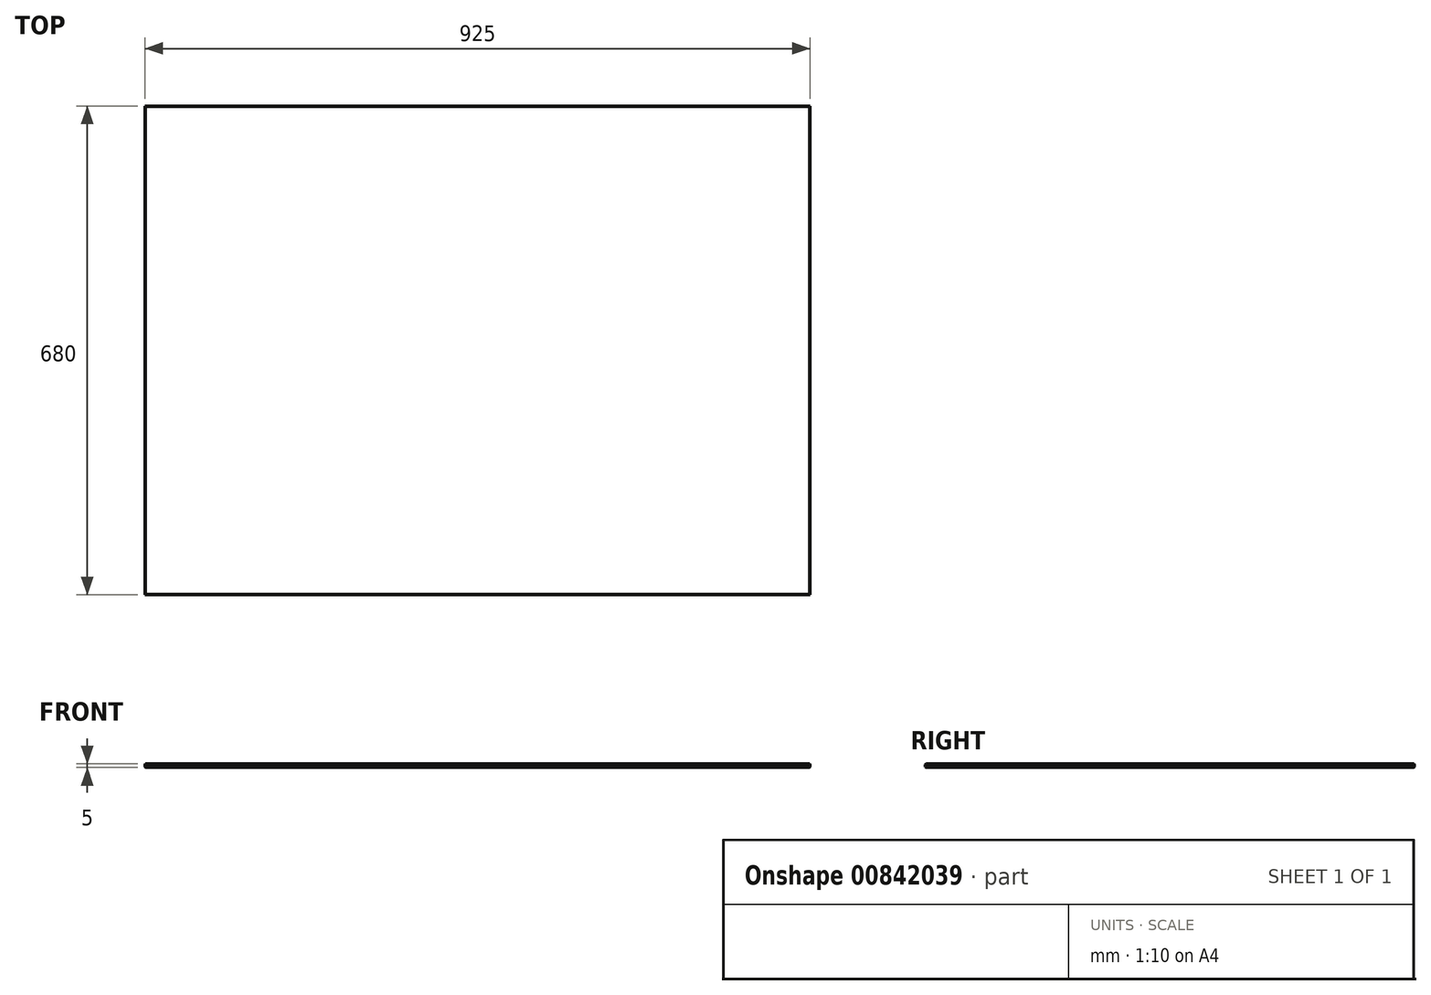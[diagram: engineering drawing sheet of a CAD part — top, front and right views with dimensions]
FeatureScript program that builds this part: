
annotation { "Feature Type Name" : "Feature", "Feature Type Description" : "" }
export const myFeature = defineFeature(function(context is Context, id is Id, definition is map)
    precondition{}
    {
        {
            var Q0;
            Q0=qCreatedBy(makeId("Top.planeOp"),FACE);
            var sketch = newSketch(context, id + "F0", { "sketchPlane" : qUnion([Q0])});
            skLineSegment(sketch, "E0.bottom", {"start": v(-462.5, 340) * mm, "end": v(462.5, 340) * mm});
            skLineSegment(sketch, "E0.top", {"start": v(-462.5, -340) * mm, "end": v(462.5, -340) * mm});
            skLineSegment(sketch, "E0.left", {"start": v(-462.5, 340) * mm, "end": v(-462.5, -340) * mm});
            skLineSegment(sketch, "E0.right", {"start": v(462.5, 340) * mm, "end": v(462.5, -340) * mm});
            skPoint(sketch, "E0.middle", {"position": v(0, 0) * mm});
            skSolve(sketch);
        }
        {
            var Q0;
            Q0=makeQuery(id+"F0.imprint","IMPRINT",FACE,{"disambiguationData":[TD([[makeQuery(id+"F0.imprint","IMPRINT",EDGE,{"derivedFrom":sQuery(id+"F0.wireOp",EDGE,"E0.bottom")}),-1.0]])]});
            extrude(context, id + "F1", {"entities" : qUnion([Q0]), "endBound" : BoundingType.SYMMETRIC, "depth" : 5 * mm, "offsetDistance" : 25 * mm});
        }
        {
            var Q0;
            Q0=makeQuery(id+"F1.opExtrude","CAP_EDGE",EDGE,{"disambiguationData":[OSD([sQuery(id+"F0.wireOp",EDGE,"E0.top")])],"isStart":false});
            var Q1;
            Q1=makeQuery(id+"F1.opExtrude","CAP_EDGE",EDGE,{"disambiguationData":[OSD([sQuery(id+"F0.wireOp",EDGE,"E0.right")])],"isStart":false});
            var Q2;
            Q2=makeQuery(id+"F1.opExtrude","CAP_EDGE",EDGE,{"disambiguationData":[OSD([sQuery(id+"F0.wireOp",EDGE,"E0.bottom")])],"isStart":false});
            var Q3;
            Q3=makeQuery(id+"F1.opExtrude","CAP_EDGE",EDGE,{"disambiguationData":[OSD([sQuery(id+"F0.wireOp",EDGE,"E0.left")])],"isStart":false});
            chamfer(context, id + "F2", {"entities" : qUnion([Q0, Q1, Q2, Q3]), "width" : 1 * mm, "tangentPropagation" : true});
        }
        {
            var Q0;
            Q0=makeQuery(id+"F1.opExtrude","CAP_EDGE",EDGE,{"disambiguationData":[OSD([sQuery(id+"F0.wireOp",EDGE,"E0.bottom")])],"isStart":true});
            var Q1;
            Q1=makeQuery(id+"F1.opExtrude","CAP_EDGE",EDGE,{"disambiguationData":[OSD([sQuery(id+"F0.wireOp",EDGE,"E0.right")])],"isStart":true});
            var Q2;
            Q2=makeQuery(id+"F1.opExtrude","CAP_EDGE",EDGE,{"disambiguationData":[OSD([sQuery(id+"F0.wireOp",EDGE,"E0.top")])],"isStart":true});
            var Q3;
            {var subQ0=sQuery(id+"F0.wireOp",EDGE,"E0.left");var subQ1=sQuery(id+"F0.wireOp",EDGE,"E0.top");Q3=makeQuery(id+"FTvvwQJVVW01trm_1.boolean.opBoolean","SPLIT",EDGE,{"disambiguationData":[TD([makeQuery(id+"F1.opExtrude","SWEPT_FACE",FACE,{"disambiguationData":[OSD([subQ1])]})])],"derivedFrom":makeQuery(id+"F1.opExtrude","CAP_EDGE",EDGE,{"disambiguationData":[OSD([subQ0])],"isStart":true})});}
            var Q4;
            Q4=makeQuery(id+"FTvvwQJVVW01trm_1.boolean.opBoolean","INTERSECT",EDGE,{"derivedFrom":[makeQuery(id+"F1.opExtrude","CAP_FACE",FACE,{"disambiguationData":[OSD([sQuery(id+"F0.wireOp",EDGE,"E0.bottom"),sQuery(id+"F0.wireOp",EDGE,"E0.top"),sQuery(id+"F0.wireOp",EDGE,"E0.left"),sQuery(id+"F0.wireOp",EDGE,"E0.right")])],"isStart":true}),makeQuery(id+"FTvvwQJVVW01trm_1.opExtrude","SWEPT_FACE",FACE,{"disambiguationData":[OSD([sQuery(id+"F6HuXMAPVFmF3pw_1.wireOp",EDGE,"e0631c99-2111-4fe0-8ead-4c3e5ad401a1.top")])]})]});
            var Q5;
            Q5=makeQuery(id+"FTvvwQJVVW01trm_1.boolean.opBoolean","INTERSECT",EDGE,{"derivedFrom":[makeQuery(id+"F1.opExtrude","CAP_FACE",FACE,{"disambiguationData":[OSD([sQuery(id+"F0.wireOp",EDGE,"E0.bottom"),sQuery(id+"F0.wireOp",EDGE,"E0.top"),sQuery(id+"F0.wireOp",EDGE,"E0.left"),sQuery(id+"F0.wireOp",EDGE,"E0.right")])],"isStart":true}),makeQuery(id+"FTvvwQJVVW01trm_1.opExtrude","SWEPT_FACE",FACE,{"disambiguationData":[OSD([sQuery(id+"F6HuXMAPVFmF3pw_1.wireOp",EDGE,"e0631c99-2111-4fe0-8ead-4c3e5ad401a1.right")])]})]});
            var Q6;
            Q6=makeQuery(id+"FTvvwQJVVW01trm_1.boolean.opBoolean","INTERSECT",EDGE,{"derivedFrom":[makeQuery(id+"F1.opExtrude","CAP_FACE",FACE,{"disambiguationData":[OSD([sQuery(id+"F0.wireOp",EDGE,"E0.bottom"),sQuery(id+"F0.wireOp",EDGE,"E0.top"),sQuery(id+"F0.wireOp",EDGE,"E0.left"),sQuery(id+"F0.wireOp",EDGE,"E0.right")])],"isStart":true}),makeQuery(id+"FTvvwQJVVW01trm_1.opExtrude","SWEPT_FACE",FACE,{"disambiguationData":[OSD([sQuery(id+"F6HuXMAPVFmF3pw_1.wireOp",EDGE,"e0631c99-2111-4fe0-8ead-4c3e5ad401a1.bottom")])]})]});
            var Q7;
            {var subQ0=sQuery(id+"F0.wireOp",EDGE,"E0.bottom");var subQ1=sQuery(id+"F0.wireOp",EDGE,"E0.left");Q7=makeQuery(id+"FTvvwQJVVW01trm_1.boolean.opBoolean","SPLIT",EDGE,{"disambiguationData":[TD([makeQuery(id+"F1.opExtrude","SWEPT_FACE",FACE,{"disambiguationData":[OSD([subQ0])]})])],"derivedFrom":makeQuery(id+"F1.opExtrude","CAP_EDGE",EDGE,{"disambiguationData":[OSD([subQ1])],"isStart":true})});}
            chamfer(context, id + "F3", {"entities" : qUnion([Q0, Q1, Q2, Q3, Q4, Q5, Q6, Q7]), "width" : 1 * mm, "tangentPropagation" : true});
        }
    });
